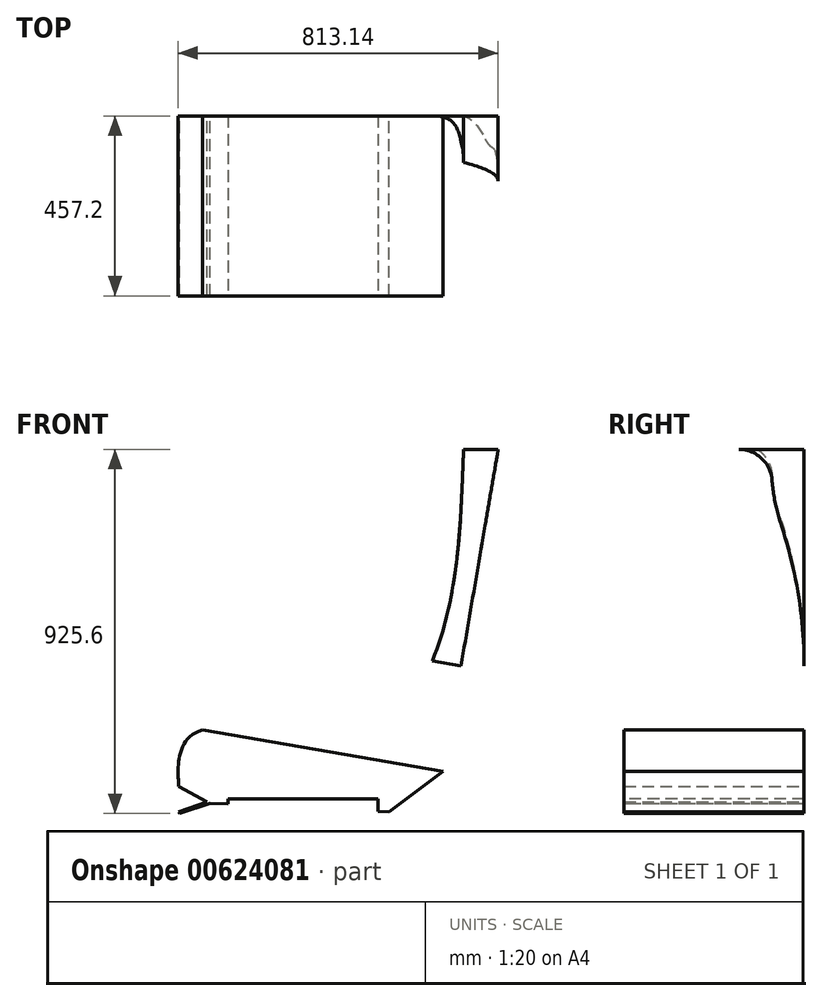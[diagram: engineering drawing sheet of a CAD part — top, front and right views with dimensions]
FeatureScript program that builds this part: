
annotation { "Feature Type Name" : "Feature", "Feature Type Description" : "" }
export const myFeature = defineFeature(function(context is Context, id is Id, definition is map)
    precondition{}
    {
        {
            var Q0;
            Q0=qCreatedBy(makeId("Front.planeOp"),FACE);
            var sketch = newSketch(context, id + "F0", { "sketchPlane" : qUnion([Q0])});
            skLineSegment(sketch, "E0", {"start": v(0, 0) * mm, "end": v(72.2, 24.38) * mm});
            skLineSegment(sketch, "E1", {"start": v(72.2, 24.38) * mm, "end": v(0, 64.25) * mm});
            skLineSegment(sketch, "E2", {"start": v(0, 0) * mm, "end": v(1.67, -4.93) * mm});
            skLineSegment(sketch, "E3", {"start": v(1.67, -4.93) * mm, "end": v(79.74, 21.43) * mm});
            skFitSpline(sketch, "E4", {"points": [v(0, 64.25) * mm, v(0, 125.44) * mm, v(47.98, 203.2) * mm, v(405.22, 172.72) * mm, v(539.44, 158.67) * mm], "startDerivative": vector(-19.62, 318.32) * mm, "endDerivative": vector(74.74, -79.6) * mm});
            skFitSpline(sketch, "E5", {"points": [v(539.44, 158.67) * mm, v(681.78, 499.41) * mm, v(723.9, 920.67) * mm], "startDerivative": vector(287.52, 606.24) * mm, "endDerivative": vector(29.77, 628.07) * mm});
            skLineSegment(sketch, "E6", {"start": v(723.9, 920.67) * mm, "end": v(811.67, 920.67) * mm});
            skLineSegment(sketch, "E7", {"start": v(811.67, 920.67) * mm, "end": v(671.25, 102.73) * mm});
            skLineSegment(sketch, "E8", {"start": v(671.25, 102.73) * mm, "end": v(534.34, 0) * mm});
            skLineSegment(sketch, "E9", {"start": v(534.34, 0) * mm, "end": v(79.74, 21.43) * mm});
            skSolve(sketch);
        }
        {
            var Q0;
            Q0=makeQuery(id+"F0.imprint","IMPRINT",FACE,{"disambiguationData":[TD([[makeQuery(id+"F0.imprint","IMPRINT",EDGE,{"derivedFrom":sQuery(id+"F0.wireOp",EDGE,"E0")}),-1.0]])]});
            extrude(context, id + "F1", {"entities" : qUnion([Q0]), "depth" : 457.2 * mm, "offsetDistance" : 25.4 * mm});
        }
        {
            var Q0;
            Q0=makeQuery(id+"F1.opExtrude","SWEPT_FACE",FACE,{"disambiguationData":[OSD([sQuery(id+"F0.wireOp",EDGE,"E7")])]});
            var sketch = newSketch(context, id + "F2", { "sketchPlane" : qUnion([Q0])});
            skArc(sketch, "E10", {"start": v(-291.18, 1044.73) * mm, "mid": v(-348.57, 1022.3) * mm, "end": v(-375.53, 966.9) * mm});
            skArc(sketch, "E11", {"start": v(-399.34, 848.62) * mm, "mid": v(-383.93, 907.05) * mm, "end": v(-375.53, 966.9) * mm});
            skArc(sketch, "E12", {"start": v(-399.34, 848.62) * mm, "mid": v(-442.64, 669.94) * mm, "end": v(-457.2, 486.65) * mm});
            skLineSegment(sketch, "E13", {"start": v(-291.18, 1044.73) * mm, "end": v(-457.2, 1044.73) * mm});
            skLineSegment(sketch, "E14", {"start": v(-457.2, 1044.73) * mm, "end": v(-457.2, 486.65) * mm});
            skLineSegment(sketch, "E15", {"start": v(-228.6, 994.92) * mm, "end": v(-228.6, 518.27) * mm, "construction": true});
            skPoint(sketch, "E15.startSnap0", {"position": v(-228.6, 1044.73) * mm});
            skArc(sketch, "E16.MirrorCS", {"start": v(-57.86, 848.62) * mm, "mid": v(-73.27, 907.05) * mm, "end": v(-81.67, 966.9) * mm});
            skArc(sketch, "E17.MirrorCS", {"start": v(-166.02, 1044.73) * mm, "mid": v(-108.63, 1022.3) * mm, "end": v(-81.67, 966.9) * mm});
            skLineSegment(sketch, "E18.MirrorCS", {"start": v(-166.02, 1044.73) * mm, "end": v(0, 1044.73) * mm});
            skLineSegment(sketch, "E19.MirrorCS", {"start": v(0, 1044.73) * mm, "end": v(0, 486.65) * mm});
            skArc(sketch, "E20.MirrorCS", {"start": v(-57.86, 848.62) * mm, "mid": v(-14.56, 669.94) * mm, "end": v(0, 486.65) * mm});
            skSolve(sketch);
        }
        {
            var Q0;
            Q0=makeQuery(id+"F2.imprint","IMPRINT",FACE,{"disambiguationData":[TD([[makeQuery(id+"F2.imprint","IMPRINT",EDGE,{"derivedFrom":sQuery(id+"F2.wireOp",EDGE,"E10")}),-1.0]])]});
            var Q1;
            Q1=makeQuery(id+"F2.imprint","IMPRINT",FACE,{"disambiguationData":[TD([[makeQuery(id+"F2.imprint","IMPRINT",EDGE,{"derivedFrom":sQuery(id+"F2.wireOp",EDGE,"E16.MirrorCS")}),-1.0]])]});
            extrude(context, id + "F3", {"entities" : qUnion([Q0, Q1]), "operationType" : NewBodyOperationType.REMOVE, "endBound" : BoundingType.THROUGH_ALL, "oppositeDirection" : true, "depth" : 25.4 * mm, "offsetDistance" : 25.4 * mm});
        }
        {
            var Q0;
            Q0=makeQuery(id+"F1.opExtrude","CAP_FACE",FACE,{"disambiguationData":[OSD([sQuery(id+"F0.wireOp",EDGE,"E0"),sQuery(id+"F0.wireOp",EDGE,"E1"),sQuery(id+"F0.wireOp",EDGE,"E2"),sQuery(id+"F0.wireOp",EDGE,"E3"),sQuery(id+"F0.wireOp",EDGE,"E4"),sQuery(id+"F0.wireOp",EDGE,"E5"),sQuery(id+"F0.wireOp",EDGE,"E6"),sQuery(id+"F0.wireOp",EDGE,"E7"),sQuery(id+"F0.wireOp",EDGE,"E8"),sQuery(id+"F0.wireOp",EDGE,"E9")])],"isStart":false});
            var sketch = newSketch(context, id + "F4", { "sketchPlane" : qUnion([Q0])});
            skLineSegment(sketch, "E21.bottom", {"start": v(125.56, 33.12) * mm, "end": v(506.01, 33.12) * mm});
            skLineSegment(sketch, "E21.top", {"start": v(125.56, -8.84) * mm, "end": v(506.01, -8.84) * mm});
            skLineSegment(sketch, "E21.left", {"start": v(125.56, 33.12) * mm, "end": v(125.56, -8.84) * mm});
            skLineSegment(sketch, "E21.right", {"start": v(506.01, 33.12) * mm, "end": v(506.01, -8.84) * mm});
            skSolve(sketch);
        }
        {
            var Q0;
            {var subQ0=sQuery(id+"F4.wireOp",EDGE,"E21.bottom");Q0=makeQuery(id+"F4.imprint","IMPRINT",FACE,{"disambiguationData":[TD([[makeQuery(id+"F4.imprint","IMPRINT",EDGE,{"derivedFrom":subQ0}),-1.0]])]});}
            extrude(context, id + "F5", {"entities" : qUnion([Q0]), "operationType" : NewBodyOperationType.REMOVE, "endBound" : BoundingType.THROUGH_ALL, "oppositeDirection" : true, "depth" : 25.4 * mm, "offsetDistance" : 25.4 * mm});
        }
    });
